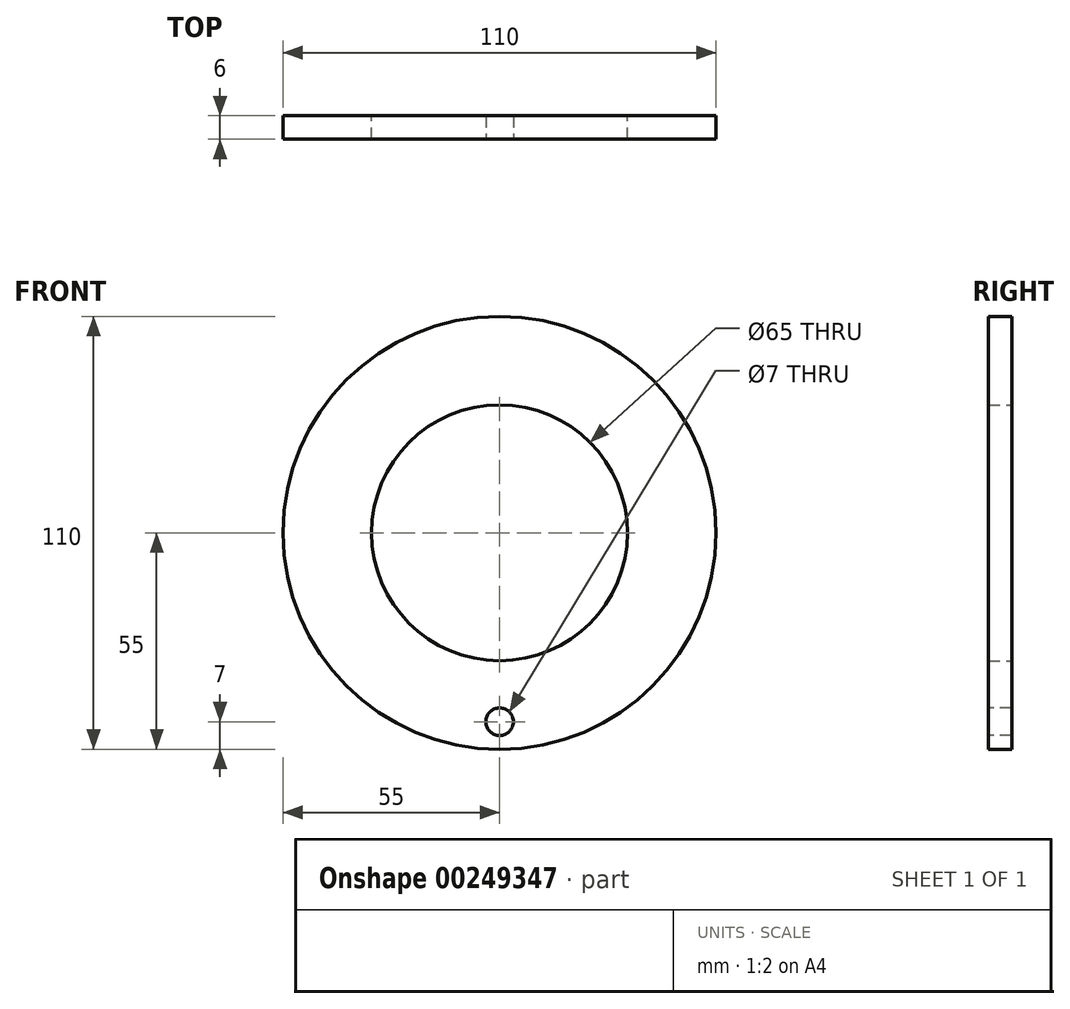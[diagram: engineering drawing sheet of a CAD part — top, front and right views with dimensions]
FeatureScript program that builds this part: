
annotation { "Feature Type Name" : "Feature", "Feature Type Description" : "" }
export const myFeature = defineFeature(function(context is Context, id is Id, definition is map)
    precondition{}
    {
        {
            var Q0;
            Q0=qCreatedBy(makeId("Front.planeOp"),FACE);
            var sketch = newSketch(context, id + "F0", { "sketchPlane" : qUnion([Q0])});
            skCircle(sketch, "E0", {"center": v(0, 0) * mm, "radius": 55 * mm});
            skCircle(sketch, "E1", {"center": v(0, 0) * mm, "radius": 32.5 * mm});
            skSolve(sketch);
        }
        {
            var Q0;
            Q0=makeQuery(id+"F0.imprint","IMPRINT",FACE,{"disambiguationData":[TD([[makeQuery(id+"F0.imprint","IMPRINT",EDGE,{"derivedFrom":sQuery(id+"F0.wireOp",EDGE,"E0")}),1.0]])]});
            extrude(context, id + "F1", {"entities" : qUnion([Q0]), "offsetDistance" : 25 * mm, "depth" : 6 * mm, "symmetric" : true});
        }
        {
            var Q0;
            Q0=qCreatedBy(makeId("Front.planeOp"),FACE);
            var sketch = newSketch(context, id + "F2", { "sketchPlane" : qUnion([Q0])});
            skCircle(sketch, "E2", {"center": v(0, -48) * mm, "radius": 3.5 * mm});
            skSolve(sketch);
        }
        {
            var Q0;
            Q0=qSketchRegion(id+"F2",true);
            extrude(context, id + "F3", {"entities" : qUnion([Q0]), "operationType" : NewBodyOperationType.REMOVE, "oppositeDirection" : true, "depth" : 25 * mm, "symmetric" : true});
        }
        {
            var Q0;
            Q0=qCreatedBy(makeId("Front.planeOp"),FACE);
            var sketch = newSketch(context, id + "F4", { "sketchPlane" : qUnion([Q0])});
            skLineSegment(sketch, "E3", {"start": v(0, 0) * mm, "end": v(15.92, 59.4) * mm, "construction": true});
            skCircle(sketch, "E4", {"center": v(15.92, 59.4) * mm, "radius": 4.5 * mm});
            skSolve(sketch);
        }
        {
            var Q0;
            Q0=qSketchRegion(id+"F4",true);
            extrude(context, id + "F5", {"entities" : qUnion([Q0]), "operationType" : NewBodyOperationType.REMOVE, "oppositeDirection" : true, "depth" : 25 * mm, "symmetric" : true});
        }
    });
